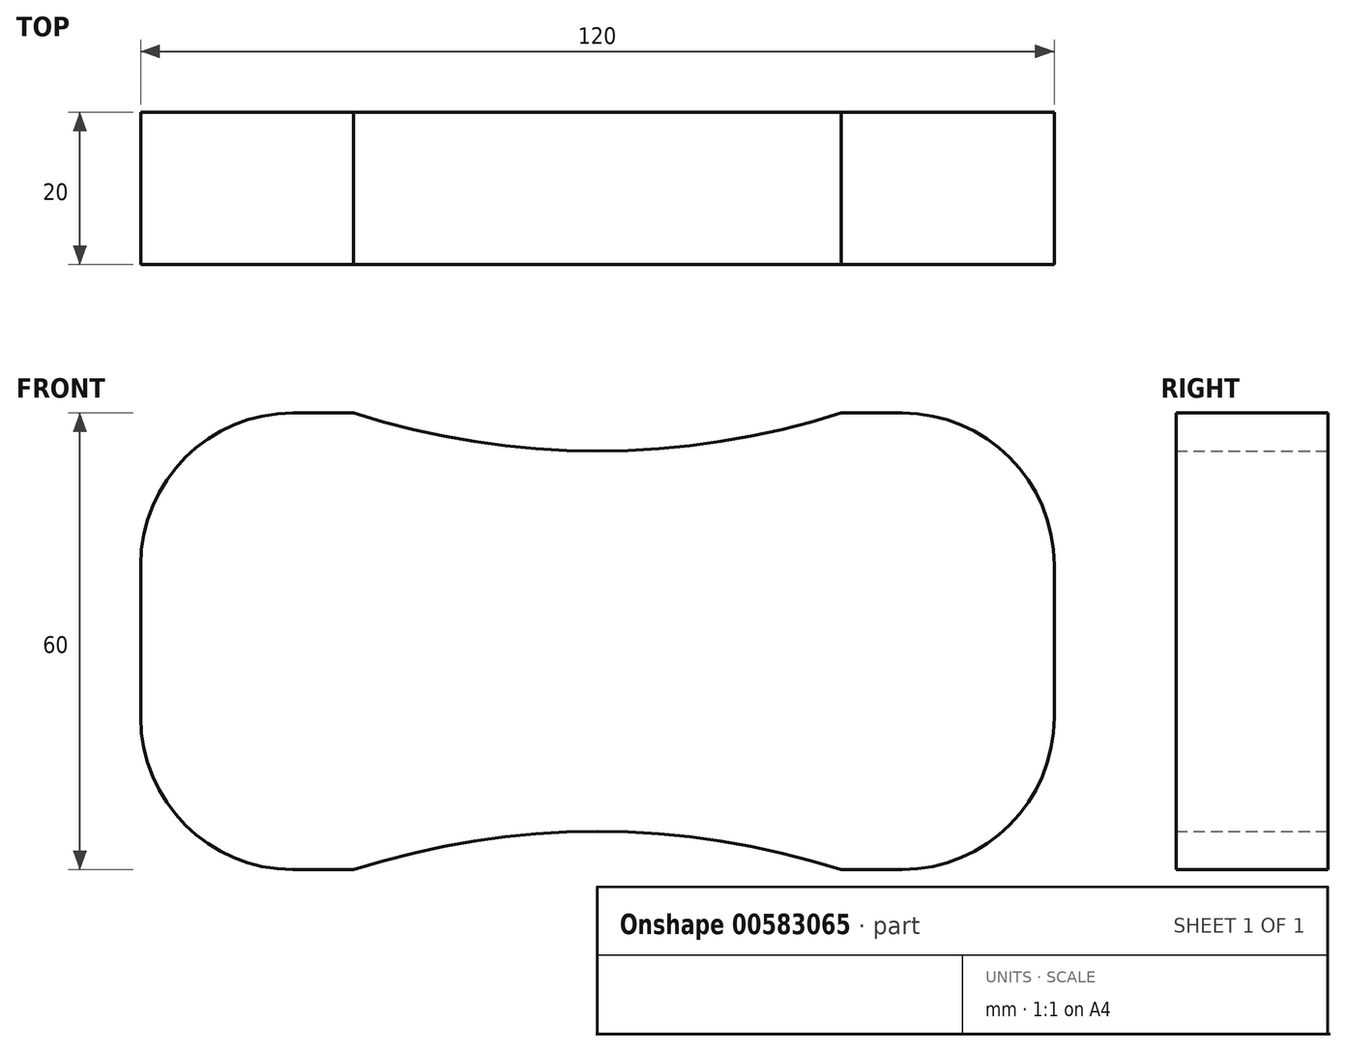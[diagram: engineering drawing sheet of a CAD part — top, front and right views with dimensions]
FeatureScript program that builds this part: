
annotation { "Feature Type Name" : "Feature", "Feature Type Description" : "" }
export const myFeature = defineFeature(function(context is Context, id is Id, definition is map)
    precondition{}
    {
        {
            var Q0;
            Q0=qCreatedBy(makeId("Front.planeOp"),FACE);
            var sketch = newSketch(context, id + "F0", { "sketchPlane" : qUnion([Q0])});
            skLineSegment(sketch, "E0", {"start": v(0, 0) * mm, "end": v(100, 0) * mm});
            skLineSegment(sketch, "E1", {"start": v(120, 20) * mm, "end": v(120, 40) * mm});
            skLineSegment(sketch, "E2", {"start": v(100, 60) * mm, "end": v(0, 60) * mm});
            skLineSegment(sketch, "E3", {"start": v(0, 40) * mm, "end": v(0, 20) * mm});
            skLineSegment(sketch, "E4", {"start": v(20, 60) * mm, "end": v(60, 60) * mm});
            skLineSegment(sketch, "E5", {"start": v(60, 60) * mm, "end": v(60, 160) * mm});
            skArc(sketch, "E6", {"start": v(27.98, 60) * mm, "mid": v(60, 55) * mm, "end": v(92.02, 60) * mm});
            skLineSegment(sketch, "E7", {"start": v(20, 0) * mm, "end": v(60, 0) * mm});
            skLineSegment(sketch, "E8", {"start": v(60, 0) * mm, "end": v(60, -100) * mm});
            skArc(sketch, "E9", {"start": v(92.02, 0) * mm, "mid": v(60, 5) * mm, "end": v(27.98, 0) * mm});
            skPoint(sketch, "E10.visualSharp", {"position": v(120, 60) * mm});
            skArc(sketch, "E11.filletArc", {"start": v(120, 40) * mm, "mid": v(114.14, 54.14) * mm, "end": v(100, 60) * mm});
            skPoint(sketch, "E12.visualSharp", {"position": v(120, 0) * mm});
            skArc(sketch, "E12.filletArc", {"start": v(100, 0) * mm, "mid": v(114.14, 5.86) * mm, "end": v(120, 20) * mm});
            skPoint(sketch, "E13.visualSharp", {"position": v(0, 0) * mm});
            skArc(sketch, "E13.filletArc", {"start": v(0, 20) * mm, "mid": v(5.86, 5.86) * mm, "end": v(20, 0) * mm});
            skPoint(sketch, "E14.visualSharp", {"position": v(0, 60) * mm});
            skArc(sketch, "E14.filletArc", {"start": v(20, 60) * mm, "mid": v(5.86, 54.14) * mm, "end": v(0, 40) * mm});
            skSolve(sketch);
        }
        {
            var Q0;
            {var subQ2=sQuery(id+"F0.wireOp",EDGE,"E1");Q0=makeQuery(id+"F0.imprint","IMPRINT",FACE,{"disambiguationData":[TD([[makeQuery(id+"F0.imprint","IMPRINT",EDGE,{"derivedFrom":subQ2}),1.0]])]});}
            extrude(context, id + "F1", {"entities" : qUnion([Q0]), "depth" : 20 * mm, "offsetDistance" : 25 * mm});
        }
    });
